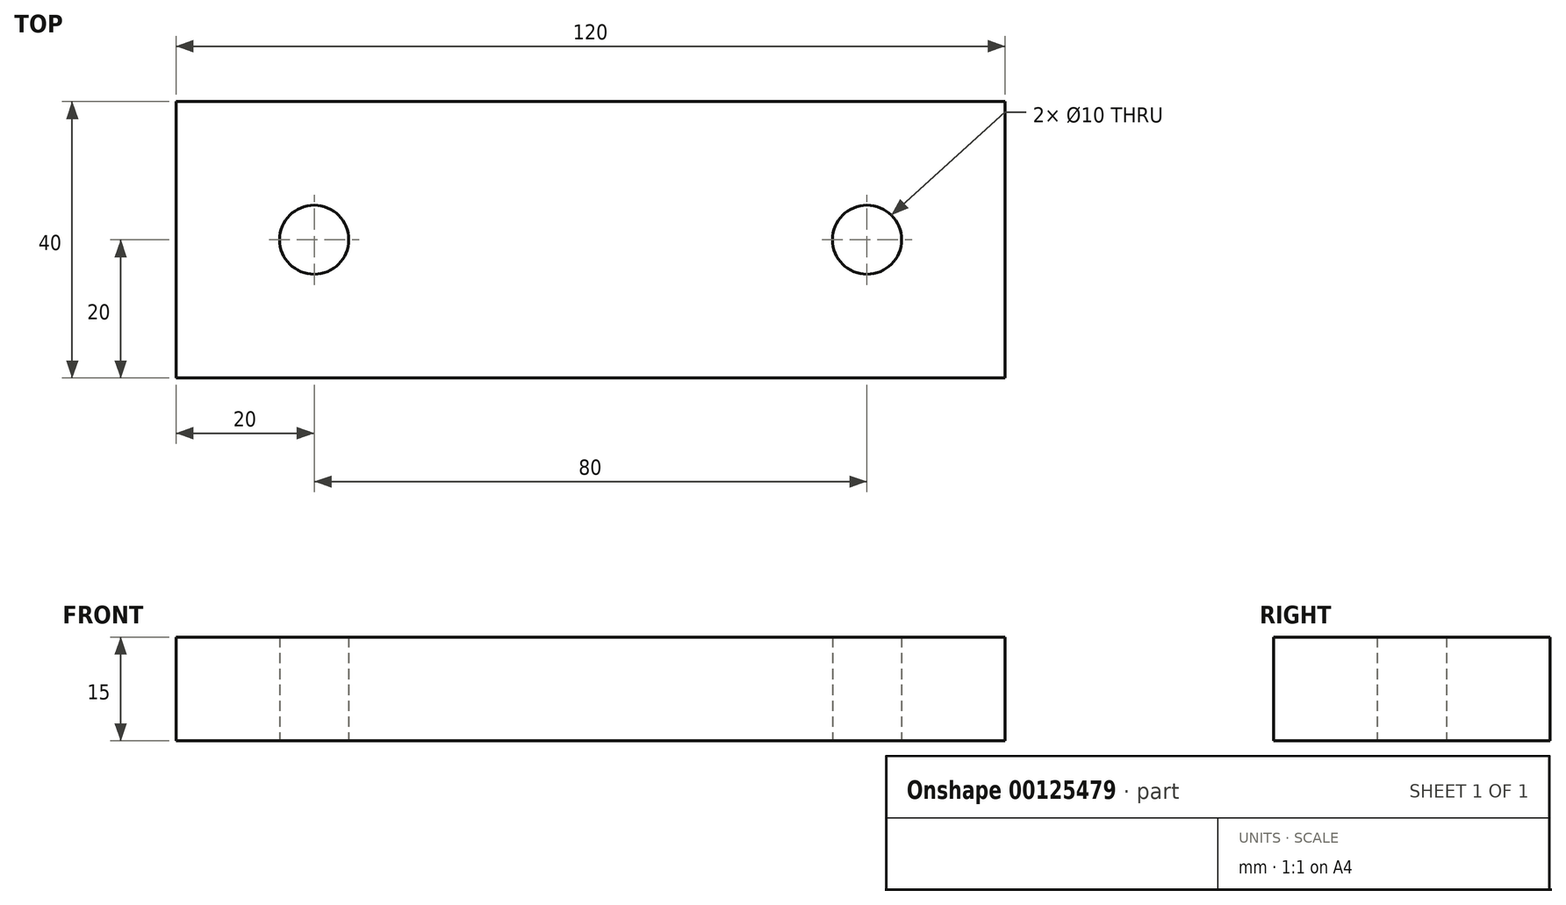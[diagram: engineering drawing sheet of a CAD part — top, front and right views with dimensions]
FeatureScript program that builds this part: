
annotation { "Feature Type Name" : "Feature", "Feature Type Description" : "" }
export const myFeature = defineFeature(function(context is Context, id is Id, definition is map)
    precondition{}
    {
        {
            var Q0;
            Q0=qCreatedBy(makeId("Top.planeOp"),FACE);
            var sketch = newSketch(context, id + "F0", { "sketchPlane" : qUnion([Q0])});
            skLineSegment(sketch, "E0.bottom", {"start": v(0, 0) * mm, "end": v(120, 0) * mm});
            skLineSegment(sketch, "E0.top", {"start": v(0, 40) * mm, "end": v(120, 40) * mm});
            skLineSegment(sketch, "E0.left", {"start": v(0, 0) * mm, "end": v(0, 40) * mm});
            skLineSegment(sketch, "E0.right", {"start": v(120, 0) * mm, "end": v(120, 40) * mm});
            skSolve(sketch);
        }
        {
            var Q0;
            Q0=qCreatedBy(makeId("Top.planeOp"),FACE);
            var sketch = newSketch(context, id + "F1", { "sketchPlane" : qUnion([Q0])});
            skLineSegment(sketch, "E1.bottom", {"start": v(0, 0) * mm, "end": v(120, 0) * mm, "construction": true});
            skLineSegment(sketch, "E1.top", {"start": v(0, 40) * mm, "end": v(120, 40) * mm, "construction": true});
            skLineSegment(sketch, "E1.left", {"start": v(0, 0) * mm, "end": v(0, 40) * mm, "construction": true});
            skLineSegment(sketch, "E1.right", {"start": v(120, 0) * mm, "end": v(120, 40) * mm, "construction": true});
            skCircle(sketch, "E2", {"center": v(20, 20) * mm, "radius": 5 * mm});
            skCircle(sketch, "E3", {"center": v(100, 20) * mm, "radius": 5 * mm});
            skSolve(sketch);
        }
        {
            var Q0;
            Q0 = qSketchRegion(id + "F0", true);
            extrude(context, id + "F2", {"entities" : qUnion([Q0]), "depth" : 15 * mm});
        }
        {
            var Q0;
            Q0 = qSketchRegion(id + "F1", true);
            extrude(context, id + "F3", {"entities" : qUnion([Q0]), "operationType" : NewBodyOperationType.REMOVE, "depth" : 25 * mm});
        }
    });
